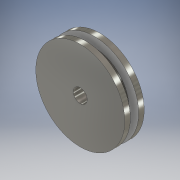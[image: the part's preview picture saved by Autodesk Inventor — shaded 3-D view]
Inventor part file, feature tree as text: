
AUTODESK INVENTOR PART (.ipt)
format: ipt  version: 2017 (Build 210142000, 142)  size: 125,952 bytes
history: native  units: mm
features: extrude x4, sketch x4
ambient origin geometry x8: Origin, YZ Plane, XZ Plane, XY Plane, X Axis, Y Axis, Z Axis, Center Point
bodies: Solid1 (feature_tree)
feature tree (8):
  extrude  "Extrusion1"  Depth=3.0mm TaperAngle=0.0deg
  extrude  "Extrusion2"  Depth=2.0mm TaperAngle=0.0deg
  extrude  "Extrusion3"  Depth=2.0mm TaperAngle=0.0deg
  extrude  "Extrusion4"  Depth=2.0mm TaperAngle=0.0deg
  sketch  "Sketch1"  dims[d0=25.0mm d1=3.0mm d2=0.0mm]
  sketch  "Sketch2"  dims[d3=32.0mm d4=2.0mm d5=0.0mm]
  sketch  "Sketch3"  dims[d6=32.0mm d7=2.0mm d8=0.0mm]
  sketch  "Sketch4"  dims[d9=5.0mm d10=2.0mm d11=0.0mm]
